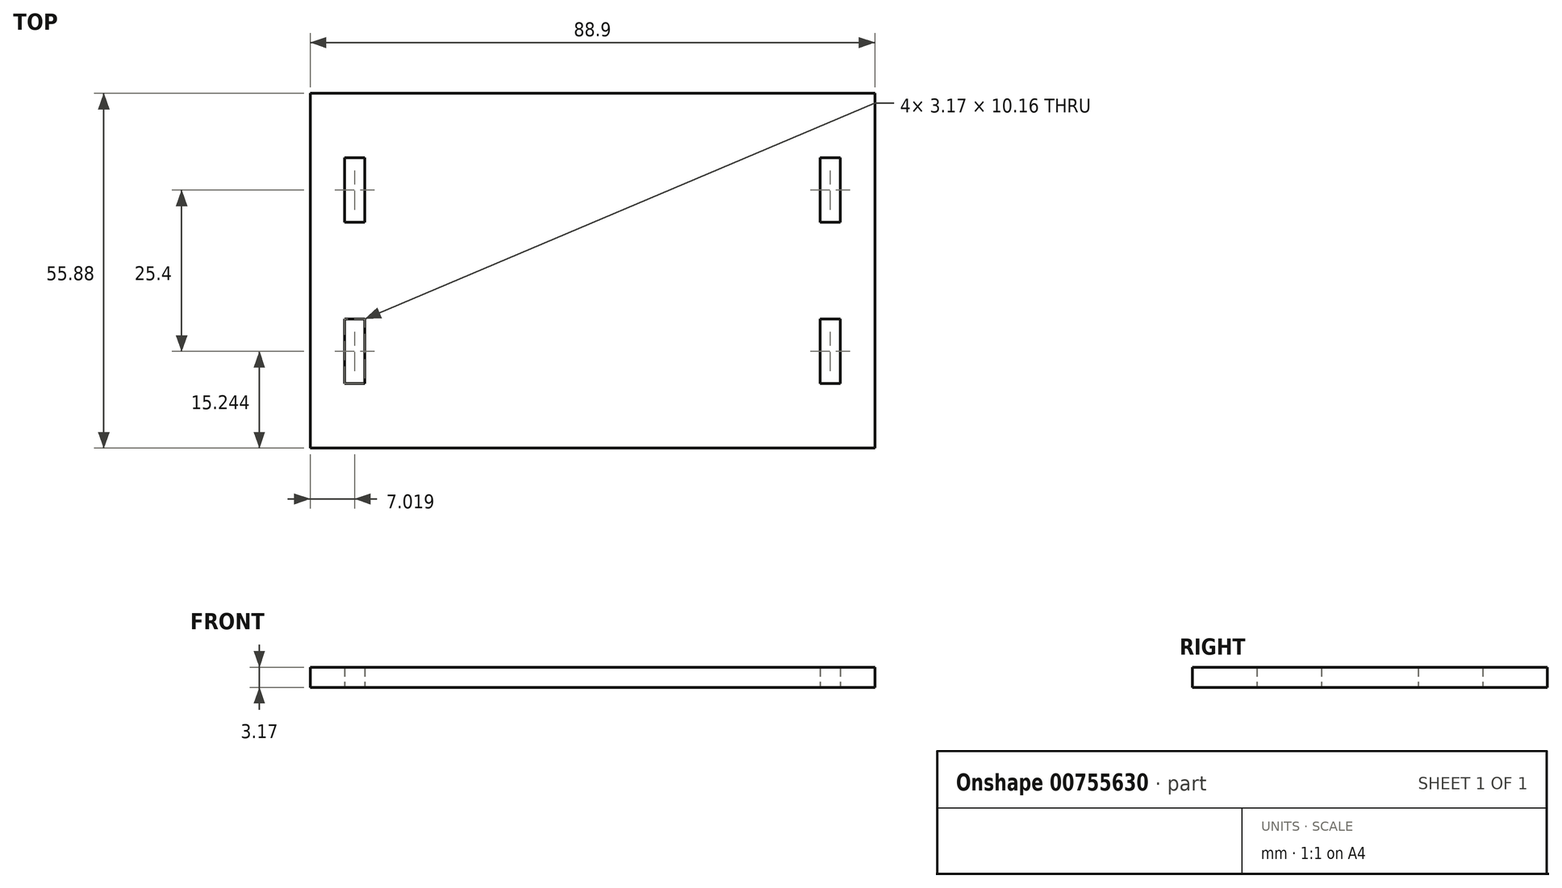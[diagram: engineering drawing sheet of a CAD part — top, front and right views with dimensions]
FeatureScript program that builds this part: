
annotation { "Feature Type Name" : "Feature", "Feature Type Description" : "" }
export const myFeature = defineFeature(function(context is Context, id is Id, definition is map)
    precondition{}
    {
        {
            var Q0;
            Q0=qCreatedBy(makeId("Top.planeOp"),FACE);
            var sketch = newSketch(context, id + "F0", { "sketchPlane" : qUnion([Q0])});
            skLineSegment(sketch, "E0.bottom", {"start": v(-44.45, 28.06) * mm, "end": v(44.45, 28.06) * mm});
            skLineSegment(sketch, "E0.top", {"start": v(-44.45, -27.82) * mm, "end": v(44.45, -27.82) * mm});
            skLineSegment(sketch, "E0.left", {"start": v(-44.45, 28.06) * mm, "end": v(-44.45, -27.82) * mm});
            skLineSegment(sketch, "E0.right", {"start": v(44.45, 28.06) * mm, "end": v(44.45, -27.82) * mm});
            skLineSegment(sketch, "E1", {"start": v(0, 28.06) * mm, "end": v(0, -27.82) * mm});
            skLineSegment(sketch, "E2", {"start": v(-44.45, 0.12) * mm, "end": v(44.45, 0.12) * mm});
            skLineSegment(sketch, "E3.bottom", {"start": v(-39.02, 17.9) * mm, "end": v(-35.84, 17.9) * mm});
            skLineSegment(sketch, "E3.top", {"start": v(-39.02, 7.74) * mm, "end": v(-35.84, 7.74) * mm});
            skLineSegment(sketch, "E3.left", {"start": v(-39.02, 17.9) * mm, "end": v(-39.02, 7.74) * mm});
            skLineSegment(sketch, "E3.right", {"start": v(-35.84, 17.9) * mm, "end": v(-35.84, 7.74) * mm});
            skLineSegment(sketch, "E4.MirrorCS", {"start": v(39.02, 17.9) * mm, "end": v(39.02, 7.74) * mm});
            skLineSegment(sketch, "E5.MirrorCS", {"start": v(35.84, 17.9) * mm, "end": v(35.84, 7.74) * mm});
            skLineSegment(sketch, "E6", {"start": v(35.84, 17.9) * mm, "end": v(39.02, 17.9) * mm});
            skLineSegment(sketch, "E7", {"start": v(39.02, 7.74) * mm, "end": v(35.84, 7.74) * mm});
            skLineSegment(sketch, "E8.MirrorCS", {"start": v(-39.02, -17.66) * mm, "end": v(-39.02, -7.5) * mm});
            skLineSegment(sketch, "E9.MirrorCS", {"start": v(-35.84, -17.66) * mm, "end": v(-35.84, -7.5) * mm});
            skLineSegment(sketch, "E10.MirrorCS", {"start": v(35.84, -17.66) * mm, "end": v(35.84, -7.5) * mm});
            skLineSegment(sketch, "E11.MirrorCS", {"start": v(39.02, -17.66) * mm, "end": v(39.02, -7.5) * mm});
            skLineSegment(sketch, "E12", {"start": v(-39.02, -7.5) * mm, "end": v(-35.84, -7.5) * mm});
            skLineSegment(sketch, "E13", {"start": v(-35.84, -17.66) * mm, "end": v(-39.02, -17.66) * mm});
            skLineSegment(sketch, "E14", {"start": v(35.84, -7.5) * mm, "end": v(39.02, -7.5) * mm});
            skLineSegment(sketch, "E15", {"start": v(39.02, -17.66) * mm, "end": v(35.84, -17.66) * mm});
            skSolve(sketch);
        }
        {
            var Q0;
            Q0=qSketchRegion(id+"F0",true);
            extrude(context, id + "F1", {"entities" : qUnion([Q0]), "depth" : 3.17 * mm, "offsetDistance" : 25.4 * mm});
        }
    });
